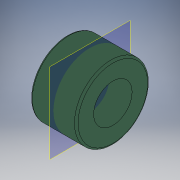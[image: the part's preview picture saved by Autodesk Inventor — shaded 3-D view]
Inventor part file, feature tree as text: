
AUTODESK INVENTOR PART (.ipt)
format: ipt  version: 2018 (Build 220112000, 112)  size: 133,632 bytes
history: native  units: mm
features: extrude x1, fillet x1, plane x1, sketch x1
ambient origin geometry x8: Origin, YZ Plane, XZ Plane, XY Plane, X Axis, Y Axis, Z Axis, Center Point
bodies: Solid1 (feature_tree)
feature tree (4):
  extrude  "Extrusion1"  Depth=0.2mm
  fillet  "Fillet1"  Radius=5.0mm
  plane  "Work Plane1"
  sketch  "Sketch1"  dims[d0=8.0mm d1=4.2mm d2=5.0mm d3=0.0mm d4=0.2mm]
